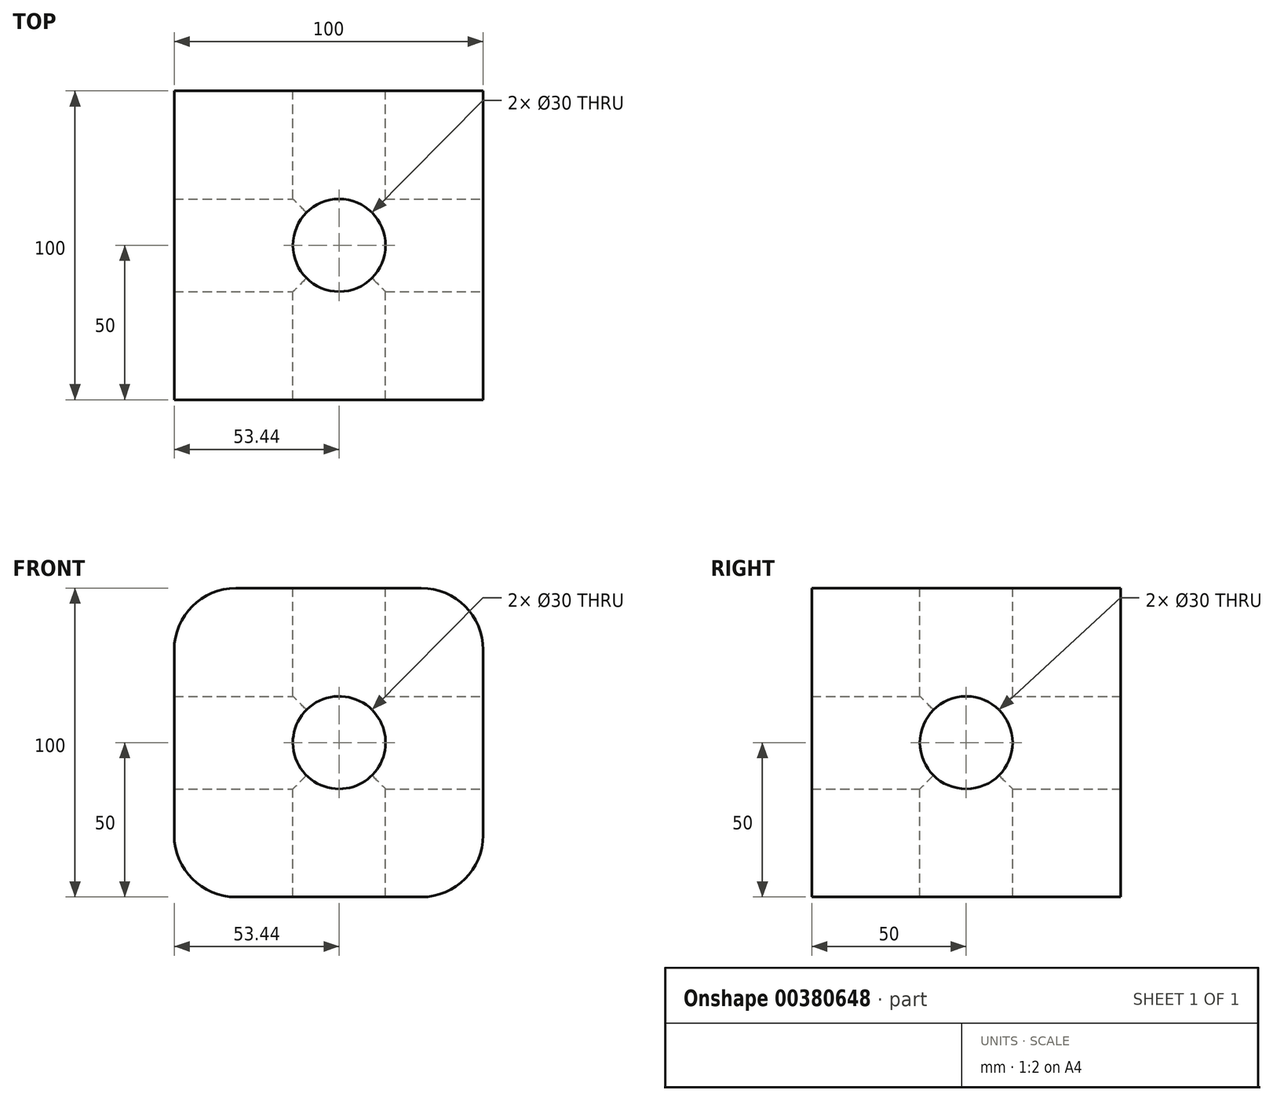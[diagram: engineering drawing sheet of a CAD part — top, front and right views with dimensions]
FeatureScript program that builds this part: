
annotation { "Feature Type Name" : "Feature", "Feature Type Description" : "" }
export const myFeature = defineFeature(function(context is Context, id is Id, definition is map)
    precondition{}
    {
        {
            var Q0;
            Q0=qCreatedBy(makeId("Front.planeOp"),FACE);
            var sketch = newSketch(context, id + "F0", { "sketchPlane" : qUnion([Q0])});
            skLineSegment(sketch, "E0.bottom", {"start": v(26.56, 50) * mm, "end": v(-33.44, 50) * mm});
            skLineSegment(sketch, "E0.top", {"start": v(26.56, -50) * mm, "end": v(-33.44, -50) * mm});
            skLineSegment(sketch, "E0.left", {"start": v(46.56, 30) * mm, "end": v(46.56, -30) * mm});
            skLineSegment(sketch, "E0.right", {"start": v(-53.44, 30) * mm, "end": v(-53.44, -30) * mm});
            skPoint(sketch, "E0.middle", {"position": v(-3.44, 0) * mm});
            skPoint(sketch, "E1.visualSharp", {"position": v(-53.44, 50) * mm});
            skArc(sketch, "E1.filletArc", {"start": v(-33.44, 50) * mm, "mid": v(-47.58, 44.14) * mm, "end": v(-53.44, 30) * mm});
            skPoint(sketch, "E2.visualSharp", {"position": v(46.56, 50) * mm});
            skArc(sketch, "E2.filletArc", {"start": v(46.56, 30) * mm, "mid": v(40.7, 44.14) * mm, "end": v(26.56, 50) * mm});
            skPoint(sketch, "E3.visualSharp", {"position": v(46.56, -50) * mm});
            skArc(sketch, "E3.filletArc", {"start": v(26.56, -50) * mm, "mid": v(40.7, -44.14) * mm, "end": v(46.56, -30) * mm});
            skPoint(sketch, "E4.visualSharp", {"position": v(-53.44, -50) * mm});
            skArc(sketch, "E4.filletArc", {"start": v(-53.44, -30) * mm, "mid": v(-47.58, -44.14) * mm, "end": v(-33.44, -50) * mm});
            skSolve(sketch);
        }
        {
            var Q0;
            Q0 = qSketchRegion(id + "F0", true);
            extrude(context, id + "F1", {"entities" : qUnion([Q0]), "depth" : 100 * mm});
        }
        {
            var Q0;
            Q0=makeQuery(id+"F1.opExtrude","SWEPT_FACE",FACE,{"disambiguationData":[OSD([sQuery(id+"F0.wireOp",EDGE,"E0.bottom")])]});
            var sketch = newSketch(context, id + "F2", { "sketchPlane" : qUnion([Q0])});
            skCircle(sketch, "E5", {"center": v(0, -50) * mm, "radius": 15 * mm});
            skPoint(sketch, "E5.centerSnap0", {"position": v(26.56, -50) * mm});
            skSolve(sketch);
        }
        {
            var Q0;
            Q0 = qSketchRegion(id + "F2", true);
            extrude(context, id + "F3", {"entities" : qUnion([Q0]), "operationType" : NewBodyOperationType.REMOVE, "endBound" : BoundingType.THROUGH_ALL, "oppositeDirection" : true, "depth" : 25.4 * mm});
        }
        {
            var Q0;
            Q0=makeQuery(id+"F1.opExtrude","CAP_FACE",FACE,{"disambiguationData":[OSD([sQuery(id+"F0.wireOp",EDGE,"E0.bottom"),sQuery(id+"F0.wireOp",EDGE,"E0.top"),sQuery(id+"F0.wireOp",EDGE,"E0.left"),sQuery(id+"F0.wireOp",EDGE,"E0.right"),sQuery(id+"F0.wireOp",EDGE,"E1.filletArc"),sQuery(id+"F0.wireOp",EDGE,"E2.filletArc"),sQuery(id+"F0.wireOp",EDGE,"E3.filletArc"),sQuery(id+"F0.wireOp",EDGE,"E4.filletArc")])],"isStart":true});
            var sketch = newSketch(context, id + "F4", { "sketchPlane" : qUnion([Q0])});
            skCircle(sketch, "E6", {"center": v(0, 0) * mm, "radius": 15 * mm});
            skSolve(sketch);
        }
        {
            var Q0;
            Q0 = qSketchRegion(id + "F4", true);
            extrude(context, id + "F5", {"entities" : qUnion([Q0]), "operationType" : NewBodyOperationType.REMOVE, "endBound" : BoundingType.THROUGH_ALL, "oppositeDirection" : true, "depth" : 25.4 * mm});
        }
        {
            var Q0;
            Q0=makeQuery(id+"F1.opExtrude","SWEPT_FACE",FACE,{"disambiguationData":[OSD([sQuery(id+"F0.wireOp",EDGE,"E0.left")])]});
            var sketch = newSketch(context, id + "F6", { "sketchPlane" : qUnion([Q0])});
            skCircle(sketch, "E7", {"center": v(-50, 0) * mm, "radius": 15 * mm});
            skPoint(sketch, "E7.centerSnap0", {"position": v(-50, -30) * mm});
            skSolve(sketch);
        }
        {
            var Q0;
            Q0 = qSketchRegion(id + "F6", true);
            extrude(context, id + "F7", {"entities" : qUnion([Q0]), "operationType" : NewBodyOperationType.REMOVE, "endBound" : BoundingType.THROUGH_ALL, "oppositeDirection" : true, "depth" : 25.4 * mm});
        }
    });
